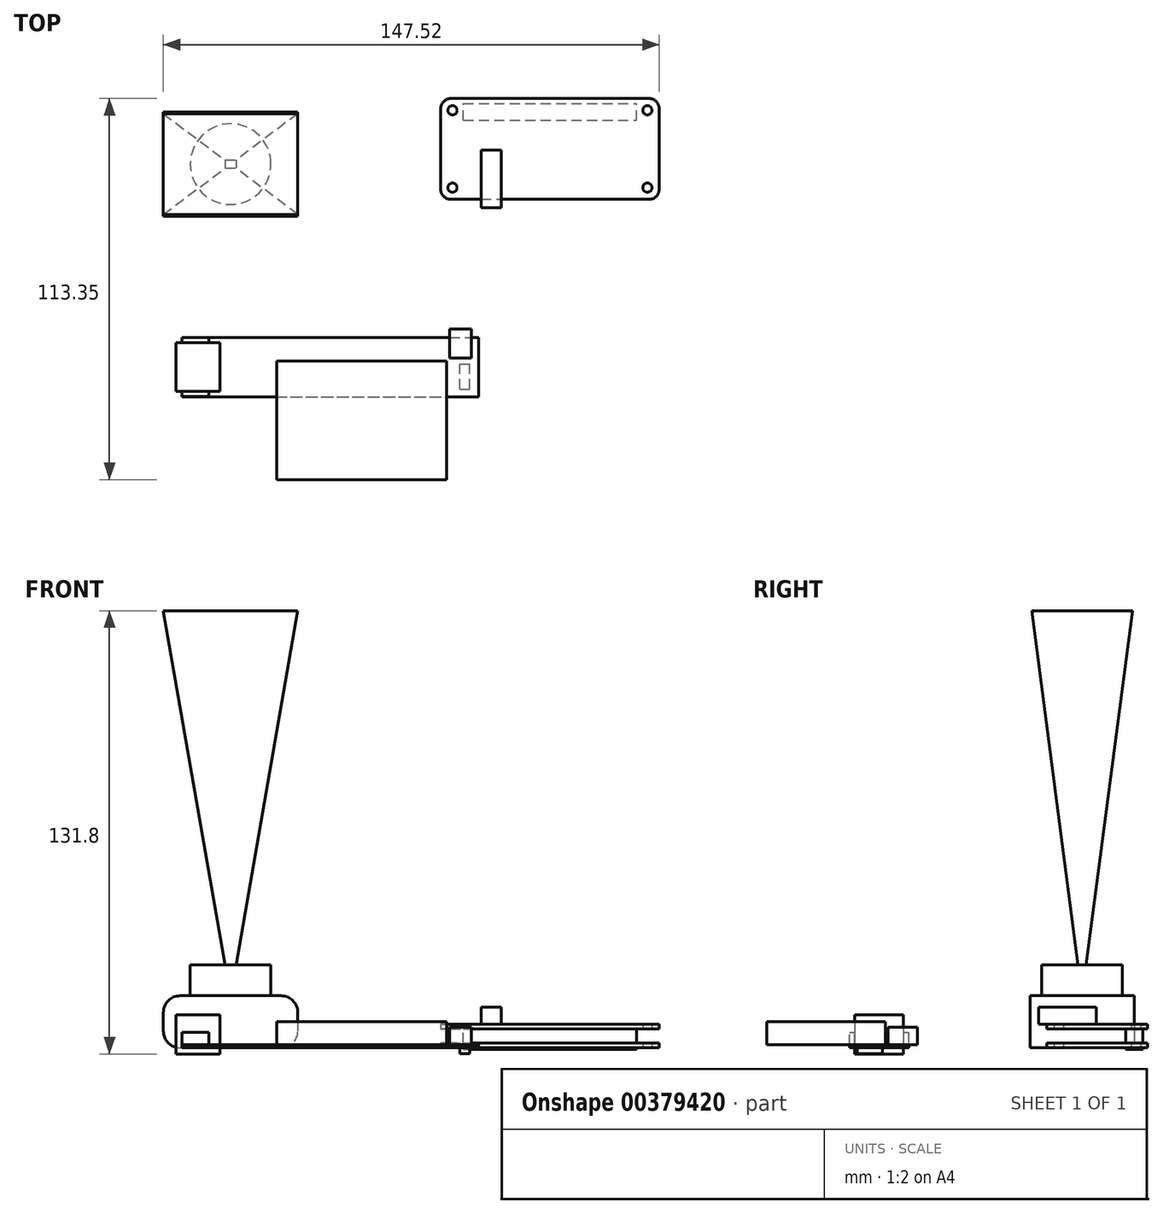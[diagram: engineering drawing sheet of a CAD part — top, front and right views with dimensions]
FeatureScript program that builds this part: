
annotation { "Feature Type Name" : "Feature", "Feature Type Description" : "" }
export const myFeature = defineFeature(function(context is Context, id is Id, definition is map)
    precondition{}
    {
        {
            var Q0;
            Q0=qCreatedBy(makeId("Top.planeOp"),FACE);
            var sketch = newSketch(context, id + "F0", { "sketchPlane" : qUnion([Q0])});
            skLineSegment(sketch, "E0.bottom", {"start": v(-54.23, 49.82) * mm, "end": v(-14.23, 49.82) * mm});
            skLineSegment(sketch, "E0.top", {"start": v(-54.23, 18.82) * mm, "end": v(-14.23, 18.82) * mm});
            skLineSegment(sketch, "E0.left", {"start": v(-54.23, 49.82) * mm, "end": v(-54.23, 18.82) * mm});
            skLineSegment(sketch, "E0.right", {"start": v(-14.23, 49.82) * mm, "end": v(-14.23, 18.82) * mm});
            skSolve(sketch);
        }
        {
            var Q0;
            Q0=makeQuery(id+"F0.imprint","IMPRINT",FACE,{"disambiguationData":[TD([[makeQuery(id+"F0.imprint","IMPRINT",EDGE,{"derivedFrom":sQuery(id+"F0.wireOp",EDGE,"E0.bottom")}),-1.0]])]});
            extrude(context, id + "F1", {"entities" : qUnion([Q0]), "depth" : 15.5 * mm});
        }
        {
            var Q0;
            Q0=makeQuery(id+"F1.opExtrude","CAP_EDGE",EDGE,{"disambiguationData":[OSD([sQuery(id+"F0.wireOp",EDGE,"E0.right")])],"isStart":false});
            var Q1;
            Q1=makeQuery(id+"F1.opExtrude","CAP_EDGE",EDGE,{"disambiguationData":[OSD([sQuery(id+"F0.wireOp",EDGE,"E0.left")])],"isStart":false});
            var Q2;
            Q2=makeQuery(id+"F1.opExtrude","CAP_EDGE",EDGE,{"disambiguationData":[OSD([sQuery(id+"F0.wireOp",EDGE,"E0.left")])],"isStart":true});
            var Q3;
            Q3=makeQuery(id+"F1.opExtrude","CAP_EDGE",EDGE,{"disambiguationData":[OSD([sQuery(id+"F0.wireOp",EDGE,"E0.right")])],"isStart":true});
            fillet(context, id + "F2", {"entities" : qUnion([Q0, Q1, Q2, Q3]), "radius" : 5 * mm, "tangentPropagation" : true, "allowEdgeOverflow" : false});
        }
        {
            var Q0;
            Q0=makeQuery(id+"F1.opExtrude","CAP_FACE",FACE,{"disambiguationData":[OSD([sQuery(id+"F0.wireOp",EDGE,"E0.bottom"),sQuery(id+"F0.wireOp",EDGE,"E0.top"),sQuery(id+"F0.wireOp",EDGE,"E0.left"),sQuery(id+"F0.wireOp",EDGE,"E0.right")])],"isStart":false});
            var sketch = newSketch(context, id + "F3", { "sketchPlane" : qUnion([Q0])});
            skCircle(sketch, "E1", {"center": v(-34.23, 34.32) * mm, "radius": 12 * mm});
            skSolve(sketch);
        }
        {
            var Q0;
            Q0=makeQuery(id+"F3.imprint","IMPRINT",FACE,{"disambiguationData":[TD([[makeQuery(id+"F3.imprint","IMPRINT",EDGE,{"derivedFrom":sQuery(id+"F3.wireOp",EDGE,"E1")}),1.0]])]});
            extrude(context, id + "F4", {"entities" : qUnion([Q0]), "operationType" : NewBodyOperationType.ADD, "depth" : 9.2 * mm});
        }
        {
            var Q0;
            Q0=qCreatedBy(makeId("Top.planeOp"),FACE);
            var sketch = newSketch(context, id + "F5", { "sketchPlane" : qUnion([Q0])});
            skLineSegment(sketch, "E2.bottom", {"start": v(-48.65, -17.22) * mm, "end": v(39.55, -17.22) * mm});
            skLineSegment(sketch, "E2.top", {"start": v(-48.65, -34.92) * mm, "end": v(39.55, -34.92) * mm});
            skLineSegment(sketch, "E2.left", {"start": v(-48.65, -17.22) * mm, "end": v(-48.65, -34.92) * mm});
            skLineSegment(sketch, "E2.right", {"start": v(39.55, -17.22) * mm, "end": v(39.55, -34.92) * mm});
            skSolve(sketch);
        }
        {
            var Q0;
            Q0=makeQuery(id+"F5.imprint","IMPRINT",FACE,{"disambiguationData":[TD([[makeQuery(id+"F5.imprint","IMPRINT",EDGE,{"derivedFrom":sQuery(id+"F5.wireOp",EDGE,"E2.bottom")}),-1.0]])]});
            extrude(context, id + "F6", {"entities" : qUnion([Q0]), "depth" : 1 * mm});
        }
        {
            var Q0;
            Q0=makeQuery(id+"F6.opExtrude","CAP_FACE",FACE,{"disambiguationData":[OSD([sQuery(id+"F5.wireOp",EDGE,"E2.bottom"),sQuery(id+"F5.wireOp",EDGE,"E2.top"),sQuery(id+"F5.wireOp",EDGE,"E2.left"),sQuery(id+"F5.wireOp",EDGE,"E2.right")])],"isStart":false});
            var sketch = newSketch(context, id + "F7", { "sketchPlane" : qUnion([Q0])});
            skLineSegment(sketch, "E3.bottom", {"start": v(-20.45, -24.22) * mm, "end": v(30.05, -24.22) * mm});
            skLineSegment(sketch, "E3.top", {"start": v(-20.45, -37.72) * mm, "end": v(30.05, -37.72) * mm});
            skLineSegment(sketch, "E3.left", {"start": v(-20.45, -24.22) * mm, "end": v(-20.45, -37.72) * mm});
            skLineSegment(sketch, "E3.right", {"start": v(30.05, -24.22) * mm, "end": v(30.05, -37.72) * mm});
            skSolve(sketch);
        }
        {
            var Q0;
            {var subQ0=sQuery(id+"F7.wireOp",EDGE,"E3.top");Q0=makeQuery(id+"F7.imprint","IMPRINT",FACE,{"disambiguationData":[TD([[makeQuery(id+"F7.imprint","IMPRINT",EDGE,{"derivedFrom":subQ0}),1.0]])]});}
            var Q1;
            {var subQ0=sQuery(id+"F7.wireOp",EDGE,"E3.bottom");Q1=makeQuery(id+"F7.imprint","IMPRINT",FACE,{"disambiguationData":[TD([[makeQuery(id+"F7.imprint","IMPRINT",EDGE,{"derivedFrom":subQ0}),-1.0]])]});}
            extrude(context, id + "F8", {"entities" : qUnion([Q0, Q1]), "operationType" : NewBodyOperationType.ADD, "depth" : 6.8 * mm});
        }
        {
            var Q0;
            Q0=makeQuery(id+"F8.opExtrude","SWEPT_FACE",FACE,{"disambiguationData":[OSD([sQuery(id+"F7.wireOp",EDGE,"E3.top")])]});
            extrude(context, id + "F9", {"entities" : qUnion([Q0]), "operationType" : NewBodyOperationType.ADD, "depth" : 21.8 * mm});
        }
        {
            var Q0;
            Q0=makeQuery(id+"F6.opExtrude","CAP_FACE",FACE,{"disambiguationData":[OSD([sQuery(id+"F5.wireOp",EDGE,"E2.bottom"),sQuery(id+"F5.wireOp",EDGE,"E2.top"),sQuery(id+"F5.wireOp",EDGE,"E2.left"),sQuery(id+"F5.wireOp",EDGE,"E2.right")])],"isStart":false});
            var sketch = newSketch(context, id + "F10", { "sketchPlane" : qUnion([Q0])});
            skLineSegment(sketch, "E4.bottom", {"start": v(-50.45, -18.82) * mm, "end": v(-37.35, -18.82) * mm});
            skLineSegment(sketch, "E4.top", {"start": v(-50.45, -33.32) * mm, "end": v(-37.35, -33.32) * mm});
            skLineSegment(sketch, "E4.left", {"start": v(-50.45, -18.82) * mm, "end": v(-50.45, -33.32) * mm});
            skLineSegment(sketch, "E4.right", {"start": v(-37.35, -18.82) * mm, "end": v(-37.35, -33.32) * mm});
            skSolve(sketch);
        }
        {
            var Q0;
            Q0=makeQuery(id+"F10.imprint","IMPRINT",FACE,{"disambiguationData":[TD([[makeQuery(id+"F10.imprint","IMPRINT",EDGE,{"derivedFrom":sQuery(id+"F10.wireOp",EDGE,"E4.bottom")}),-1.0]])]});
            extrude(context, id + "F11", {"entities" : qUnion([Q0]), "operationType" : NewBodyOperationType.ADD, "depth" : 8.8 * mm});
        }
        {
            var Q0;
            Q0=makeQuery(id+"F10.imprint","IMPRINT",FACE,{"disambiguationData":[TD([[makeQuery(id+"F10.imprint","IMPRINT",EDGE,{"derivedFrom":sQuery(id+"F10.wireOp",EDGE,"E4.bottom")}),-1.0]])]});
            extrude(context, id + "F12", {"entities" : qUnion([Q0]), "operationType" : NewBodyOperationType.ADD, "oppositeDirection" : true, "depth" : 2.8 * mm});
        }
        {
            var Q0;
            Q0=makeQuery(id+"F6.opExtrude","CAP_FACE",FACE,{"disambiguationData":[OSD([sQuery(id+"F5.wireOp",EDGE,"E2.bottom"),sQuery(id+"F5.wireOp",EDGE,"E2.top"),sQuery(id+"F5.wireOp",EDGE,"E2.left"),sQuery(id+"F5.wireOp",EDGE,"E2.right")])],"isStart":false});
            var sketch = newSketch(context, id + "F13", { "sketchPlane" : qUnion([Q0])});
            skLineSegment(sketch, "E5.bottom", {"start": v(30.95, -14.72) * mm, "end": v(37.45, -14.72) * mm});
            skLineSegment(sketch, "E5.top", {"start": v(30.95, -23.39) * mm, "end": v(37.45, -23.39) * mm});
            skLineSegment(sketch, "E5.left", {"start": v(30.95, -14.72) * mm, "end": v(30.95, -23.39) * mm});
            skLineSegment(sketch, "E5.right", {"start": v(37.45, -14.72) * mm, "end": v(37.45, -23.39) * mm});
            skSolve(sketch);
        }
        {
            var Q0;
            {var subQ0=sQuery(id+"F13.wireOp",EDGE,"E5.bottom");Q0=makeQuery(id+"F13.imprint","IMPRINT",FACE,{"disambiguationData":[TD([[makeQuery(id+"F13.imprint","IMPRINT",EDGE,{"derivedFrom":subQ0}),-1.0]])]});}
            var Q1;
            {var subQ0=sQuery(id+"F13.wireOp",EDGE,"E5.top");Q1=makeQuery(id+"F13.imprint","IMPRINT",FACE,{"disambiguationData":[TD([[makeQuery(id+"F13.imprint","IMPRINT",EDGE,{"derivedFrom":subQ0}),1.0]])]});}
            extrude(context, id + "F14", {"entities" : qUnion([Q0, Q1]), "operationType" : NewBodyOperationType.ADD, "depth" : 5.2 * mm});
        }
        {
            var Q0;
            Q0=makeQuery(id+"F6.opExtrude","CAP_FACE",FACE,{"disambiguationData":[OSD([sQuery(id+"F5.wireOp",EDGE,"E2.bottom"),sQuery(id+"F5.wireOp",EDGE,"E2.top"),sQuery(id+"F5.wireOp",EDGE,"E2.left"),sQuery(id+"F5.wireOp",EDGE,"E2.right")])],"isStart":true});
            var sketch = newSketch(context, id + "F15", { "sketchPlane" : qUnion([Q0])});
            skLineSegment(sketch, "E6.bottom", {"start": v(33.93, 32.6) * mm, "end": v(36.95, 32.6) * mm});
            skLineSegment(sketch, "E6.top", {"start": v(33.93, 25.1) * mm, "end": v(36.95, 25.1) * mm});
            skLineSegment(sketch, "E6.left", {"start": v(33.93, 32.6) * mm, "end": v(33.93, 25.1) * mm});
            skLineSegment(sketch, "E6.right", {"start": v(36.95, 32.6) * mm, "end": v(36.95, 25.1) * mm});
            skSolve(sketch);
        }
        {
            var Q0;
            Q0=makeQuery(id+"F15.imprint","IMPRINT",FACE,{"disambiguationData":[TD([[makeQuery(id+"F15.imprint","IMPRINT",EDGE,{"derivedFrom":sQuery(id+"F15.wireOp",EDGE,"E6.bottom")}),-1.0]])]});
            extrude(context, id + "F16", {"entities" : qUnion([Q0]), "operationType" : NewBodyOperationType.ADD, "depth" : 1.7 * mm});
        }
        {
            var Q0;
            Q0=qCreatedBy(makeId("Top.planeOp"),FACE);
            var sketch = newSketch(context, id + "F17", { "sketchPlane" : qUnion([Q0])});
            skLineSegment(sketch, "E7.bottom", {"start": v(31.29, 53.83) * mm, "end": v(90.29, 53.83) * mm});
            skLineSegment(sketch, "E7.top", {"start": v(31.29, 23.83) * mm, "end": v(90.29, 23.83) * mm});
            skLineSegment(sketch, "E7.left", {"start": v(28.29, 50.83) * mm, "end": v(28.29, 26.83) * mm});
            skLineSegment(sketch, "E7.right", {"start": v(93.29, 50.83) * mm, "end": v(93.29, 26.83) * mm});
            skPoint(sketch, "E8.visualSharp", {"position": v(93.29, 53.83) * mm});
            skArc(sketch, "E8.filletArc", {"start": v(93.29, 50.83) * mm, "mid": v(92.4, 52.95) * mm, "end": v(90.29, 53.83) * mm});
            skPoint(sketch, "E9.visualSharp", {"position": v(93.29, 23.83) * mm});
            skArc(sketch, "E9.filletArc", {"start": v(90.29, 23.83) * mm, "mid": v(92.4, 24.7) * mm, "end": v(93.29, 26.83) * mm});
            skPoint(sketch, "E10.visualSharp", {"position": v(28.29, 23.83) * mm});
            skArc(sketch, "E10.filletArc", {"start": v(28.29, 26.83) * mm, "mid": v(29.16, 24.7) * mm, "end": v(31.29, 23.83) * mm});
            skPoint(sketch, "E11.visualSharp", {"position": v(28.29, 53.83) * mm});
            skArc(sketch, "E11.filletArc", {"start": v(31.29, 53.83) * mm, "mid": v(29.16, 52.95) * mm, "end": v(28.29, 50.83) * mm});
            skPoint(sketch, "E12", {"position": v(31.79, 27.33) * mm});
            skPoint(sketch, "E13", {"position": v(31.79, 50.33) * mm});
            skPoint(sketch, "E14", {"position": v(89.79, 50.33) * mm});
            skPoint(sketch, "E15", {"position": v(89.79, 27.33) * mm});
            skSolve(sketch);
        }
        {
            var Q0;
            Q0=makeQuery(id+"F17.imprint","IMPRINT",FACE,{"disambiguationData":[TD([[makeQuery(id+"F17.imprint","IMPRINT",EDGE,{"derivedFrom":sQuery(id+"F17.wireOp",EDGE,"E7.bottom")}),-1.0]])]});
            extrude(context, id + "F18", {"entities" : qUnion([Q0]), "depth" : 1.5 * mm});
        }
        {
            var Q0;
            Q0=qCreatedBy(makeId("Top.planeOp"),FACE);
            cPlane(context, id + "F19", {"entities" : qUnion([Q0]), "cplaneType" : CPlaneType.OFFSET, "offset" : 5.6 * mm, "width" : 150 * mm, "height" : 150 * mm});
        }
        {
            var Q0;
            Q0=qCreatedBy(id+"F19.planeOp",FACE);
            var sketch = newSketch(context, id + "F20", { "sketchPlane" : qUnion([Q0])});
            skLineSegment(sketch, "E16.bottom", {"start": v(31.29, 53.83) * mm, "end": v(90.29, 53.83) * mm});
            skLineSegment(sketch, "E16.top", {"start": v(31.29, 23.83) * mm, "end": v(90.29, 23.83) * mm});
            skLineSegment(sketch, "E16.left", {"start": v(28.29, 50.83) * mm, "end": v(28.29, 26.83) * mm});
            skLineSegment(sketch, "E16.right", {"start": v(93.29, 50.83) * mm, "end": v(93.29, 26.83) * mm});
            skPoint(sketch, "E17.visualSharp", {"position": v(93.29, 53.83) * mm});
            skArc(sketch, "E17.filletArc", {"start": v(93.29, 50.83) * mm, "mid": v(92.4, 52.95) * mm, "end": v(90.29, 53.83) * mm});
            skPoint(sketch, "E18.visualSharp", {"position": v(93.29, 23.83) * mm});
            skArc(sketch, "E18.filletArc", {"start": v(90.29, 23.83) * mm, "mid": v(92.4, 24.7) * mm, "end": v(93.29, 26.83) * mm});
            skPoint(sketch, "E19.visualSharp", {"position": v(28.29, 23.83) * mm});
            skArc(sketch, "E19.filletArc", {"start": v(28.29, 26.83) * mm, "mid": v(29.16, 24.7) * mm, "end": v(31.29, 23.83) * mm});
            skPoint(sketch, "E20.visualSharp", {"position": v(28.29, 53.83) * mm});
            skArc(sketch, "E20.filletArc", {"start": v(31.29, 53.83) * mm, "mid": v(29.16, 52.95) * mm, "end": v(28.29, 50.83) * mm});
            skPoint(sketch, "E21", {"position": v(31.79, 27.33) * mm});
            skPoint(sketch, "E22", {"position": v(31.79, 50.33) * mm});
            skPoint(sketch, "E23", {"position": v(89.79, 50.33) * mm});
            skPoint(sketch, "E24", {"position": v(89.79, 27.33) * mm});
            skSolve(sketch);
        }
        {
            var Q0;
            Q0=makeQuery(id+"F20.imprint","IMPRINT",FACE,{"disambiguationData":[TD([[makeQuery(id+"F20.imprint","IMPRINT",EDGE,{"derivedFrom":sQuery(id+"F20.wireOp",EDGE,"E16.bottom")}),-1.0]])]});
            extrude(context, id + "F21", {"entities" : qUnion([Q0]), "depth" : 1.5 * mm});
        }
        {
            var Q0;
            Q0=sQuery(id+"F17.wireOp",VERTEX,"E13");
            var Q1;
            Q1=sQuery(id+"F17.wireOp",VERTEX,"E12");
            var Q2;
            Q2=sQuery(id+"F17.wireOp",VERTEX,"E15");
            var Q3;
            Q3=sQuery(id+"F17.wireOp",VERTEX,"E14");
            var Q4;
            Q4=makeQuery(id+"F18.opExtrude","SWEPT_BODY",BODY,{"disambiguationData":[OSD([sQuery(id+"F17.wireOp",EDGE,"E7.bottom"),sQuery(id+"F17.wireOp",EDGE,"E7.top"),sQuery(id+"F17.wireOp",EDGE,"E7.left"),sQuery(id+"F17.wireOp",EDGE,"E7.right"),sQuery(id+"F17.wireOp",EDGE,"E8.filletArc"),sQuery(id+"F17.wireOp",EDGE,"E9.filletArc"),sQuery(id+"F17.wireOp",EDGE,"E10.filletArc"),sQuery(id+"F17.wireOp",EDGE,"E11.filletArc")])]});
            var Q5;
            Q5=makeQuery(id+"F21.opExtrude","SWEPT_BODY",BODY,{"disambiguationData":[OSD([sQuery(id+"F20.wireOp",EDGE,"E16.bottom"),sQuery(id+"F20.wireOp",EDGE,"E16.top"),sQuery(id+"F20.wireOp",EDGE,"E16.left"),sQuery(id+"F20.wireOp",EDGE,"E16.right"),sQuery(id+"F20.wireOp",EDGE,"E17.filletArc"),sQuery(id+"F20.wireOp",EDGE,"E18.filletArc"),sQuery(id+"F20.wireOp",EDGE,"E19.filletArc"),sQuery(id+"F20.wireOp",EDGE,"E20.filletArc")])]});
            hole(context, id + "F22", {"style" : HoleStyle.SIMPLE, "endStyle" : HoleEndStyle.THROUGH, "oppositeDirection" : true, "holeDiameter" : 2.75 * mm, "tappedDepth" : 12 * mm, "tapClearance" : 3, "locations" : qUnion([Q0, Q1, Q2, Q3]), "scope" : qUnion([Q4, Q5])});
        }
        {
            var Q0;
            Q0=makeQuery(id+"F21.opExtrude","CAP_FACE",FACE,{"disambiguationData":[OSD([sQuery(id+"F20.wireOp",EDGE,"E16.bottom"),sQuery(id+"F20.wireOp",EDGE,"E16.top"),sQuery(id+"F20.wireOp",EDGE,"E16.left"),sQuery(id+"F20.wireOp",EDGE,"E16.right"),sQuery(id+"F20.wireOp",EDGE,"E17.filletArc"),sQuery(id+"F20.wireOp",EDGE,"E18.filletArc"),sQuery(id+"F20.wireOp",EDGE,"E19.filletArc"),sQuery(id+"F20.wireOp",EDGE,"E20.filletArc")])],"isStart":true});
            var sketch = newSketch(context, id + "F23", { "sketchPlane" : qUnion([Q0])});
            skLineSegment(sketch, "E25.bottom", {"start": v(35.04, -47.33) * mm, "end": v(86.54, -47.33) * mm});
            skLineSegment(sketch, "E25.top", {"start": v(35.04, -52.33) * mm, "end": v(86.54, -52.33) * mm});
            skLineSegment(sketch, "E25.left", {"start": v(35.04, -47.33) * mm, "end": v(35.04, -52.33) * mm});
            skLineSegment(sketch, "E25.right", {"start": v(86.54, -47.33) * mm, "end": v(86.54, -52.33) * mm});
            skSolve(sketch);
        }
        {
            var Q0;
            Q0=makeQuery(id+"F23.imprint","IMPRINT",FACE,{"disambiguationData":[TD([[makeQuery(id+"F23.imprint","IMPRINT",EDGE,{"derivedFrom":sQuery(id+"F23.wireOp",EDGE,"E25.bottom")}),-1.0]])]});
            extrude(context, id + "F24", {"entities" : qUnion([Q0]), "operationType" : NewBodyOperationType.ADD, "depth" : 6 * mm});
        }
        {
            var Q0;
            Q0=makeQuery(id+"F21.opExtrude","CAP_FACE",FACE,{"disambiguationData":[OSD([sQuery(id+"F20.wireOp",EDGE,"E16.bottom"),sQuery(id+"F20.wireOp",EDGE,"E16.top"),sQuery(id+"F20.wireOp",EDGE,"E16.left"),sQuery(id+"F20.wireOp",EDGE,"E16.right"),sQuery(id+"F20.wireOp",EDGE,"E17.filletArc"),sQuery(id+"F20.wireOp",EDGE,"E18.filletArc"),sQuery(id+"F20.wireOp",EDGE,"E19.filletArc"),sQuery(id+"F20.wireOp",EDGE,"E20.filletArc")])],"isStart":false});
            var sketch = newSketch(context, id + "F25", { "sketchPlane" : qUnion([Q0])});
            skLineSegment(sketch, "E26.bottom", {"start": v(40.29, 38.53) * mm, "end": v(46.29, 38.53) * mm});
            skLineSegment(sketch, "E26.top", {"start": v(40.29, 21.33) * mm, "end": v(46.29, 21.33) * mm});
            skLineSegment(sketch, "E26.left", {"start": v(40.29, 38.53) * mm, "end": v(40.29, 21.33) * mm});
            skLineSegment(sketch, "E26.right", {"start": v(46.29, 38.53) * mm, "end": v(46.29, 21.33) * mm});
            skSolve(sketch);
        }
        {
            var Q0;
            {var subQ0=sQuery(id+"F25.wireOp",EDGE,"E26.top");Q0=makeQuery(id+"F25.imprint","IMPRINT",FACE,{"disambiguationData":[TD([[makeQuery(id+"F25.imprint","IMPRINT",EDGE,{"derivedFrom":subQ0}),1.0]])]});}
            var Q1;
            {var subQ0=sQuery(id+"F25.wireOp",EDGE,"E26.bottom");Q1=makeQuery(id+"F25.imprint","IMPRINT",FACE,{"disambiguationData":[TD([[makeQuery(id+"F25.imprint","IMPRINT",EDGE,{"derivedFrom":subQ0}),-1.0]])]});}
            extrude(context, id + "F26", {"entities" : qUnion([Q0, Q1]), "operationType" : NewBodyOperationType.ADD, "depth" : 5 * mm});
        }
        {
            var Q0;
            Q0=qCreatedBy(makeId("Top.planeOp"),FACE);
            cPlane(context, id + "F27", {"entities" : qUnion([Q0]), "cplaneType" : CPlaneType.OFFSET, "offset" : 60 * mm, "width" : 150 * mm, "height" : 150 * mm});
        }
        {
            var Q0;
            Q0=qCreatedBy(makeId("Top.planeOp"),FACE);
            cPlane(context, id + "F28", {"entities" : qUnion([Q0]), "cplaneType" : CPlaneType.OFFSET, "offset" : 95 * mm, "width" : 150 * mm, "height" : 150 * mm});
        }
        {
            var Q0;
            Q0=qCreatedBy(makeId("Top.planeOp"),FACE);
            cPlane(context, id + "F29", {"entities" : qUnion([Q0]), "cplaneType" : CPlaneType.OFFSET, "offset" : 130 * mm, "width" : 150 * mm, "height" : 150 * mm});
        }
        {
            var Q0;
            Q0=qCreatedBy(id+"F29.planeOp",FACE);
            var sketch = newSketch(context, id + "F30", { "sketchPlane" : qUnion([Q0])});
            skLineSegment(sketch, "E27.bottom", {"start": v(-14.23, 19.32) * mm, "end": v(-54.23, 19.32) * mm});
            skLineSegment(sketch, "E27.top", {"start": v(-14.23, 49.32) * mm, "end": v(-54.23, 49.32) * mm});
            skLineSegment(sketch, "E27.left", {"start": v(-14.23, 19.32) * mm, "end": v(-14.23, 49.32) * mm});
            skLineSegment(sketch, "E27.right", {"start": v(-54.23, 19.32) * mm, "end": v(-54.23, 49.32) * mm});
            skPoint(sketch, "E27.middle", {"position": v(-34.23, 34.32) * mm});
            skSolve(sketch);
        }
        {
            var Q1;
            Q1=makeQuery(id+"F30.imprint","IMPRINT",FACE,{"disambiguationData":[TD([[makeQuery(id+"F30.imprint","IMPRINT",EDGE,{"derivedFrom":sQuery(id+"F30.wireOp",EDGE,"E27.bottom")}),-1.0]])]});
            var Q2;
            Q2=sQuery(id+"F3.wireOp",VERTEX,"E1.center");
            loft(context, id + "F31", {"operationType" : NewBodyOperationType.ADD, "sheetProfilesArray" : [{ "sheetProfileEntities" : qUnion([Q1]) }, { "sheetProfileEntities" : qUnion([Q2]) }]});
        }
        {
            var Q0;
            {var subQ0=sQuery(id+"F10.wireOp",EDGE,"E4.top");Q0=makeQuery(id+"F12.boolean.opBoolean","MERGE",FACE,{"derivedFrom":[makeQuery(id+"F11.opExtrude","SWEPT_FACE",FACE,{"disambiguationData":[OSD([subQ0])]}),makeQuery(id+"F12.opExtrude","SWEPT_FACE",FACE,{"disambiguationData":[OSD([subQ0])]})]});}
            var sketch = newSketch(context, id + "F32", { "sketchPlane" : qUnion([Q0])});
            skLineSegment(sketch, "E28.bottom", {"start": v(-48.65, 1) * mm, "end": v(-40.65, 1) * mm});
            skLineSegment(sketch, "E28.top", {"start": v(-48.65, 4.6) * mm, "end": v(-40.65, 4.6) * mm});
            skLineSegment(sketch, "E28.left", {"start": v(-48.65, 1) * mm, "end": v(-48.65, 4.6) * mm});
            skLineSegment(sketch, "E28.right", {"start": v(-40.65, 1) * mm, "end": v(-40.65, 4.6) * mm});
            skSolve(sketch);
        }
        {
            var Q0;
            {var subQ0=sQuery(id+"F10.wireOp",EDGE,"E4.bottom");Q0=makeQuery(id+"F12.boolean.opBoolean","MERGE",FACE,{"derivedFrom":[makeQuery(id+"F11.opExtrude","SWEPT_FACE",FACE,{"disambiguationData":[OSD([subQ0])]}),makeQuery(id+"F12.opExtrude","SWEPT_FACE",FACE,{"disambiguationData":[OSD([subQ0])]})]});}
            var sketch = newSketch(context, id + "F33", { "sketchPlane" : qUnion([Q0])});
            skLineSegment(sketch, "E29.bottom", {"start": v(40.65, 4.6) * mm, "end": v(48.65, 4.6) * mm});
            skLineSegment(sketch, "E29.top", {"start": v(40.65, 1) * mm, "end": v(48.65, 1) * mm});
            skLineSegment(sketch, "E29.left", {"start": v(40.65, 4.6) * mm, "end": v(40.65, 1) * mm});
            skLineSegment(sketch, "E29.right", {"start": v(48.65, 4.6) * mm, "end": v(48.65, 1) * mm});
            skSolve(sketch);
        }
        {
            var Q0;
            Q0=makeQuery(id+"F32.imprint","IMPRINT",FACE,{"disambiguationData":[TD([[makeQuery(id+"F32.imprint","IMPRINT",EDGE,{"derivedFrom":sQuery(id+"F32.wireOp",EDGE,"E28.bottom")}),1.0]])]});
            var Q1;
            Q1=makeQuery(id+"F33.imprint","IMPRINT",FACE,{"disambiguationData":[TD([[makeQuery(id+"F33.imprint","IMPRINT",EDGE,{"derivedFrom":sQuery(id+"F33.wireOp",EDGE,"E29.bottom")}),-1.0]])]});
            extrude(context, id + "F34", {"entities" : qUnion([Q0, Q1]), "operationType" : NewBodyOperationType.ADD, "depth" : 3 * mm, "symmetric" : true});
        }
        {
            var Q0;
            Q0=qCreatedBy(makeId("Top.planeOp"),FACE);
            cPlane(context, id + "F35", {"entities" : qUnion([Q0]), "cplaneType" : CPlaneType.OFFSET, "offset" : 115 * mm, "width" : 150 * mm, "height" : 150 * mm});
        }
    });
